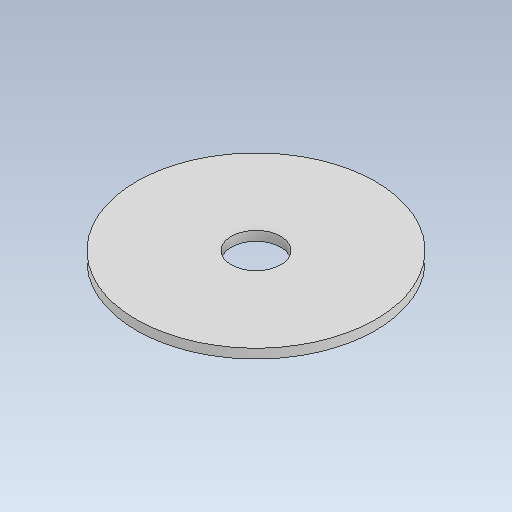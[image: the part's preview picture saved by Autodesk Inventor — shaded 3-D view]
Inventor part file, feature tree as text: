
AUTODESK INVENTOR PART (.ipt)
format: ipt  version: 2023 (Build 270158000, 158)  size: 83,456 bytes
history: native  units: in
note: dims shown in document units (in); Inventor stores cm internally (conversion verified against a paired STEP export)
features: other x3, sketch x1
ambient origin geometry x8: Origin, YZ Plane, XZ Plane, XY Plane, X Axis, Y Axis, Z Axis, Center Point
bodies: Solid1 (feature_tree)
feature tree (4):
  other  "Washer.ipt"
  other  "Solid1::Washer.ipt"
  other  "TaggingFeature1"
  sketch  "Sketch1"  dims[d0=0.3937in]
